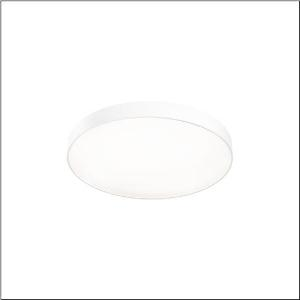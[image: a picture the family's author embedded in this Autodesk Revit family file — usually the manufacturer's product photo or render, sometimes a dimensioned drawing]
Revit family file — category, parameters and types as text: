
# Revit family: round_21_m_51mr36fd0321w
name_source: partatom
category: Lighting Fixtures
units: mm (PartAtom-declared; Revit-internal decimal feet)

## family parameters
Cut with Voids When Loaded = No
Host = Face
Light Source = No
Part Type = Normal
Room Calculation Point = No
Round Connector Dimension = Use Diameter
Shared = No

## types (1)
- Round 21 M (1 x LED, 6790 lm, 54.8 W, 3000K)
    Apparent Load = 55 VA
    CIE Flux Codes = 49 80 96 100 100
    Color Rendering = 80
    Color Temperature = 3000K
    Default Elevation = 1800 mm
    Description = Round 21 M, wall and ceiling luminaire, primary optical cover: cover, of PMMA, opal, light emission: direct distribution, primary light characteristic: symmetric, installation type: suspended mounting, surface-mounted, LED, rated luminous flux: 6.790lm, luminous efficacy: 124lm/W, light colour: 830, colour temperature: 3000K, with terminal, 5-pole, mains connection: 230V, AC, 50/60Hz, rated input power: 55W, housing, of aluminium, coated, white, diameter: 600mm, height: 62mm, protection rating (complete): IP40, insulation class (complete): insulation class I (protective earthing), certification: CE, impact resistance: IK04, permissible operating ambient temperature: -10..+35°C, packaging unit: 1 piece
    Height = 87 mm
    Lamp = 1 x LED
    Lamp Light Flux = 6790 lm
    Lamp Power = 54.8 W
    Lamp count = 1
    Length = 600 mm
    Luminous efficacy = 124 lm/W
    Manufacturer = Siteco
    ModVariant = No
    Model = 51MR36FD0321W
    Mounting Place = Ceiling
    Mounting Type = Surface mounted
    Number of Poles = 1
    OnlyDefault = Yes
    Power Factor = 1
    Product Name = Round 21 M
    Product group = wall and ceiling luminaire
    ProductGroupID = 302
    Protection Class = Protection class I
    Protection Degree = IP 40
    RLX_Detail_Level = 1
    RLX_Emergency_Light_Flux = 0 lm
    RLX_Emergency_Type = 0
    RLX_Emergency_Type_DB = No
    RlxData = <blob elided: 11697 chars, md5=9e682242>
    Socket = socket
    Standby Power = 0 W
    System Light Flux = 6790 lm
    System Power = 55 W
    Type Comments = Product without accessories
    Type Image = l_1258330.jpg
    URL = http://relux.com
    VarID = ---
    Voltage = 0 V
    Weight = 0.00 kg
    Width = 0 mm  [stored 0 ft]

note: [stored X ft] marks values corroborated as IEEE doubles in the binary element streams (Revit-internal decimal feet)

## geometry (parser evidence)
native form markers: Sweep x11
no freeform markers — native parametric forms only
